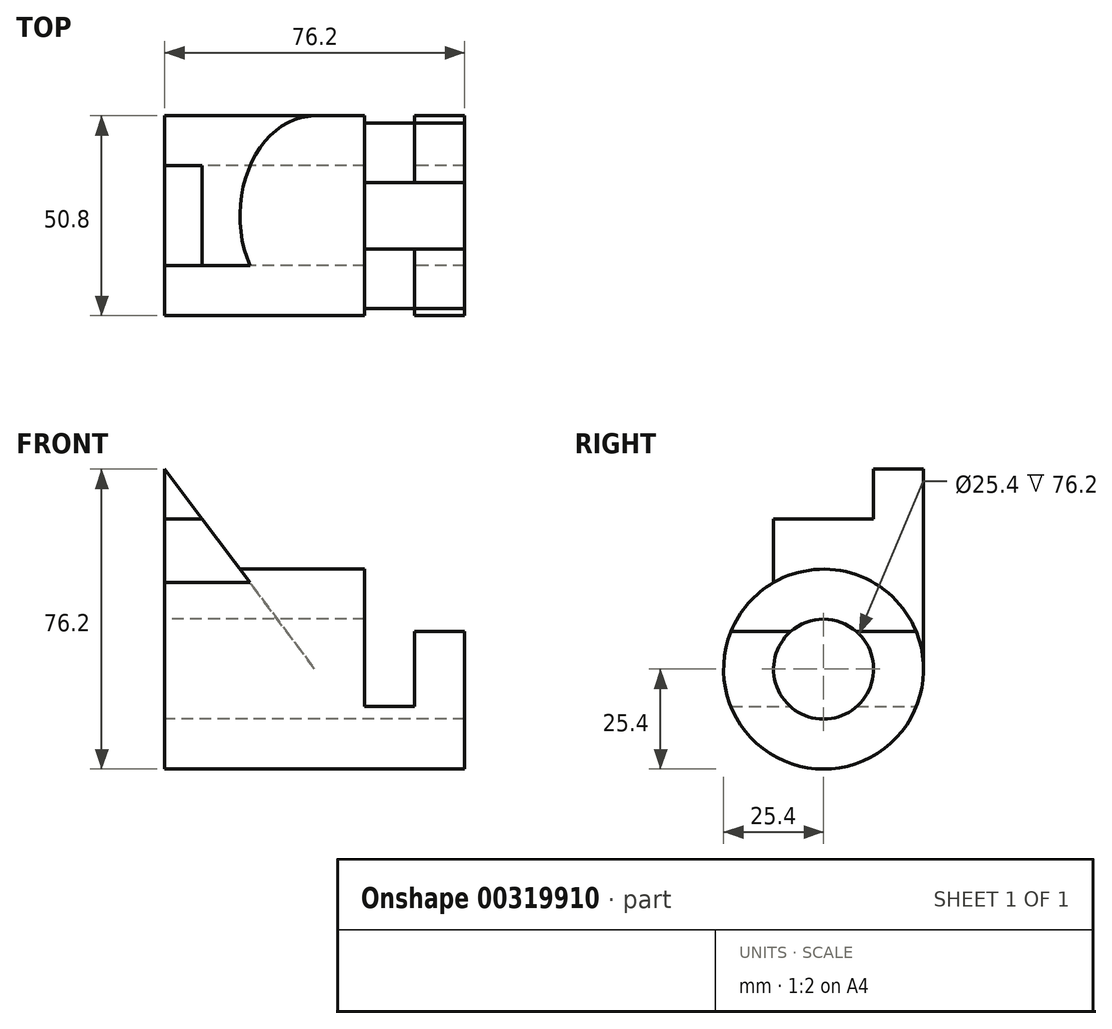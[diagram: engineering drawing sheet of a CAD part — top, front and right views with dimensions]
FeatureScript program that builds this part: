
annotation { "Feature Type Name" : "Feature", "Feature Type Description" : "" }
export const myFeature = defineFeature(function(context is Context, id is Id, definition is map)
    precondition{}
    {
        {
            var Q0;
            Q0=qCreatedBy(makeId("Right.planeOp"),FACE);
            var sketch = newSketch(context, id + "F0", { "sketchPlane" : qUnion([Q0])});
            skArc(sketch, "E0", {"start": v(-8.4, 9.52) * mm, "mid": v(0, -12.7) * mm, "end": v(8.4, 9.52) * mm});
            skArc(sketch, "E1", {"start": v(-23.55, 9.52) * mm, "mid": v(0, -25.4) * mm, "end": v(23.55, 9.52) * mm});
            skLineSegment(sketch, "E2", {"start": v(8.4, 9.52) * mm, "end": v(23.55, 9.52) * mm});
            skLineSegment(sketch, "E3", {"start": v(-8.4, 9.53) * mm, "end": v(-23.55, 9.52) * mm});
            skSolve(sketch);
        }
        {
            var Q0;
            Q0 = qSketchRegion(id + "F0", true);
            extrude(context, id + "F1", {"entities" : qUnion([Q0]), "depth" : 12.7 * mm});
        }
        {
            var Q0;
            Q0=qCreatedBy(makeId("Right.planeOp"),FACE);
            cPlane(context, id + "F2", {"entities" : qUnion([Q0]), "cplaneType" : CPlaneType.OFFSET, "offset" : 12.7 * mm, "oppositeDirection" : true, "width" : 152.4 * mm, "height" : 152.4 * mm});
        }
        {
            var Q0;
            Q0=qCreatedBy(id+"F2.planeOp",FACE);
            var sketch = newSketch(context, id + "F3", { "sketchPlane" : qUnion([Q0])});
            skCircle(sketch, "E4", {"center": v(0, 0) * mm, "radius": 25.4 * mm});
            skCircle(sketch, "E5", {"center": v(0, 0) * mm, "radius": 12.7 * mm});
            skSolve(sketch);
        }
        {
            var Q0;
            Q0 = qSketchRegion(id + "F3", true);
            extrude(context, id + "F4", {"entities" : qUnion([Q0]), "operationType" : NewBodyOperationType.ADD, "oppositeDirection" : true, "depth" : 50.8 * mm});
        }
        {
            var Q0;
            Q0=qCreatedBy(makeId("Right.planeOp"),FACE);
            var sketch = newSketch(context, id + "F5", { "sketchPlane" : qUnion([Q0])});
            skLineSegment(sketch, "E6", {"start": v(-23.55, -9.52) * mm, "end": v(-8.4, -9.52) * mm});
            skArc(sketch, "E7", {"start": v(-23.55, -9.53) * mm, "mid": v(0, -25.4) * mm, "end": v(23.55, -9.52) * mm});
            skArc(sketch, "E8", {"start": v(-8.4, -9.53) * mm, "mid": v(0, -12.7) * mm, "end": v(8.4, -9.52) * mm});
            skLineSegment(sketch, "E9.trimOffspring", {"start": v(8.4, -9.52) * mm, "end": v(23.55, -9.52) * mm});
            skSolve(sketch);
        }
        {
            var Q0;
            Q0 = qSketchRegion(id + "F5", true);
            extrude(context, id + "F6", {"entities" : qUnion([Q0]), "operationType" : NewBodyOperationType.ADD, "oppositeDirection" : true, "depth" : 12.7 * mm});
        }
        {
            var Q0;
            Q0=qCreatedBy(makeId("Front.planeOp"),FACE);
            cPlane(context, id + "F7", {"entities" : qUnion([Q0]), "cplaneType" : CPlaneType.OFFSET, "offset" : 6.35 * mm, "oppositeDirection" : true, "width" : 152.4 * mm, "height" : 152.4 * mm});
        }
        {
            var Q0;
            Q0=qCreatedBy(id+"F7.planeOp",FACE);
            var sketch = newSketch(context, id + "F8", { "sketchPlane" : qUnion([Q0])});
            skLineSegment(sketch, "E10", {"start": v(-63.5, 50.8) * mm, "end": v(-63.5, 0) * mm});
            skLineSegment(sketch, "E11", {"start": v(-63.5, 0) * mm, "end": v(-25.4, 0) * mm});
            skLineSegment(sketch, "E12", {"start": v(-25.4, 0) * mm, "end": v(-63.5, 50.8) * mm});
            skSolve(sketch);
        }
        {
            var Q0;
            Q0 = qSketchRegion(id + "F8", true);
            extrude(context, id + "F9", {"entities" : qUnion([Q0]), "operationType" : NewBodyOperationType.ADD, "endBound" : BoundingType.SYMMETRIC, "depth" : 38.1 * mm});
        }
        {
            var Q0;
            Q0=qCreatedBy(makeId("Right.planeOp"),FACE);
            var sketch = newSketch(context, id + "F10", { "sketchPlane" : qUnion([Q0])});
            skLineSegment(sketch, "E13.bottom", {"start": v(-12.7, 50.8) * mm, "end": v(12.7, 50.8) * mm});
            skLineSegment(sketch, "E13.top", {"start": v(-12.7, 38.1) * mm, "end": v(12.7, 38.1) * mm});
            skLineSegment(sketch, "E13.left", {"start": v(-12.7, 50.8) * mm, "end": v(-12.7, 38.1) * mm});
            skLineSegment(sketch, "E13.right", {"start": v(12.7, 50.8) * mm, "end": v(12.7, 38.1) * mm});
            skSolve(sketch);
        }
        {
            var Q0;
            Q0 = qSketchRegion(id + "F10", true);
            extrude(context, id + "F11", {"entities" : qUnion([Q0]), "operationType" : NewBodyOperationType.REMOVE, "endBound" : BoundingType.THROUGH_ALL, "oppositeDirection" : true, "depth" : 25.4 * mm});
        }
        {
            var Q0;
            Q0=makeQuery(id+"F9.boolean.opBoolean","MERGE",FACE,{"derivedFrom":[makeQuery(id+"F4.opExtrude","CAP_FACE",FACE,{"disambiguationData":[OSD([sQuery(id+"F3.wireOp",EDGE,"E4"),sQuery(id+"F3.wireOp",EDGE,"E5")])],"isStart":false}),makeQuery(id+"F9.opExtrude","SWEPT_FACE",FACE,{"disambiguationData":[OSD([sQuery(id+"F8.wireOp",EDGE,"E10")])]})]});
            var sketch = newSketch(context, id + "F12", { "sketchPlane" : qUnion([Q0])});
            skLineSegment(sketch, "E14.0", {"start": v(12.7, 0) * mm, "end": v(-12.7, 0) * mm});
            skArc(sketch, "E15", {"start": v(12.7, 0) * mm, "mid": v(0, 12.7) * mm, "end": v(-12.7, 0) * mm});
            skSolve(sketch);
        }
        {
            var Q0;
            Q0 = qSketchRegion(id + "F12", true);
            extrude(context, id + "F13", {"entities" : qUnion([Q0]), "operationType" : NewBodyOperationType.REMOVE, "oppositeDirection" : true, "depth" : 38.1 * mm});
        }
    });
